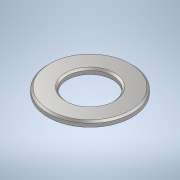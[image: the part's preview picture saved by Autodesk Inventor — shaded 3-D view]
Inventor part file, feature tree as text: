
AUTODESK INVENTOR PART (.ipt)
format: ipt  version: 2021 (Build 250183000, 183)  size: 111,104 bytes
history: native  units: mm
features: extrude x1, chamfer x1, sketch x1
ambient origin geometry x8: Origin, YZ Plane, XZ Plane, XY Plane, X Axis, Y Axis, Z Axis, Center Point
bodies: Solid1 (feature_tree)
feature tree (3):
  extrude  "Extrusion1"  Depth=1.5mm
  chamfer  "Chamfer1"  Distance=1.5mm
  sketch  "Sketch1"  dims[d0=13.0mm d1=24.0mm d2=1.5mm d3=0.0mm d4=0.5mm d5=2.0mm d6=45.0deg]
